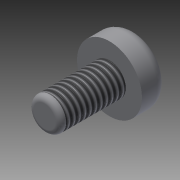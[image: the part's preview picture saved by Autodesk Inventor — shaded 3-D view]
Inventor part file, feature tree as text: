
AUTODESK INVENTOR PART (.ipt)
format: ipt  version: 2015 (Build 190159000, 159)  size: 137,728 bytes
history: native  units: mm
features: extrude x3, sketch x3, fillet x2, thread x1
ambient origin geometry x8: Origin, YZ Plane, XZ Plane, XY Plane, X Axis, Y Axis, Z Axis, Center Point
bodies: Solid1 (feature_tree)
feature tree (9):
  extrude  "Extrusion1"  Depth=6.0mm TaperAngle=0.0deg
  extrude  "Extrusion2"  Depth=2.4mm TaperAngle=0.0deg
  fillet  "Fillet4"  Radius=0.5mm
  thread  "Thread2"  [1 undecoded]
  fillet  "Fillet5"  Radius=1.0mm
  extrude  "Extrusion4"  Depth=1.0mm
  sketch  "Sketch1"  dims[d0=3.0mm d1=6.0mm d2=0.0mm]
  sketch  "Sketch2"  dims[d3=6.0mm d4=2.4mm d5=0.0mm d26=0.5mm d29=10.0mm d30=0.0mm d31=1.0mm]
  sketch  "Sketch5"  dims[d32=0.3mm d33=0.3mm d35=0.3mm d36=0.3mm d37=1.0mm d38=0.0mm]
note: 1 required parameter value undecoded (feature->parameter linkage not recoverable at this tier; creation-order binding heuristic only, values carry confidence <= 0.55)
